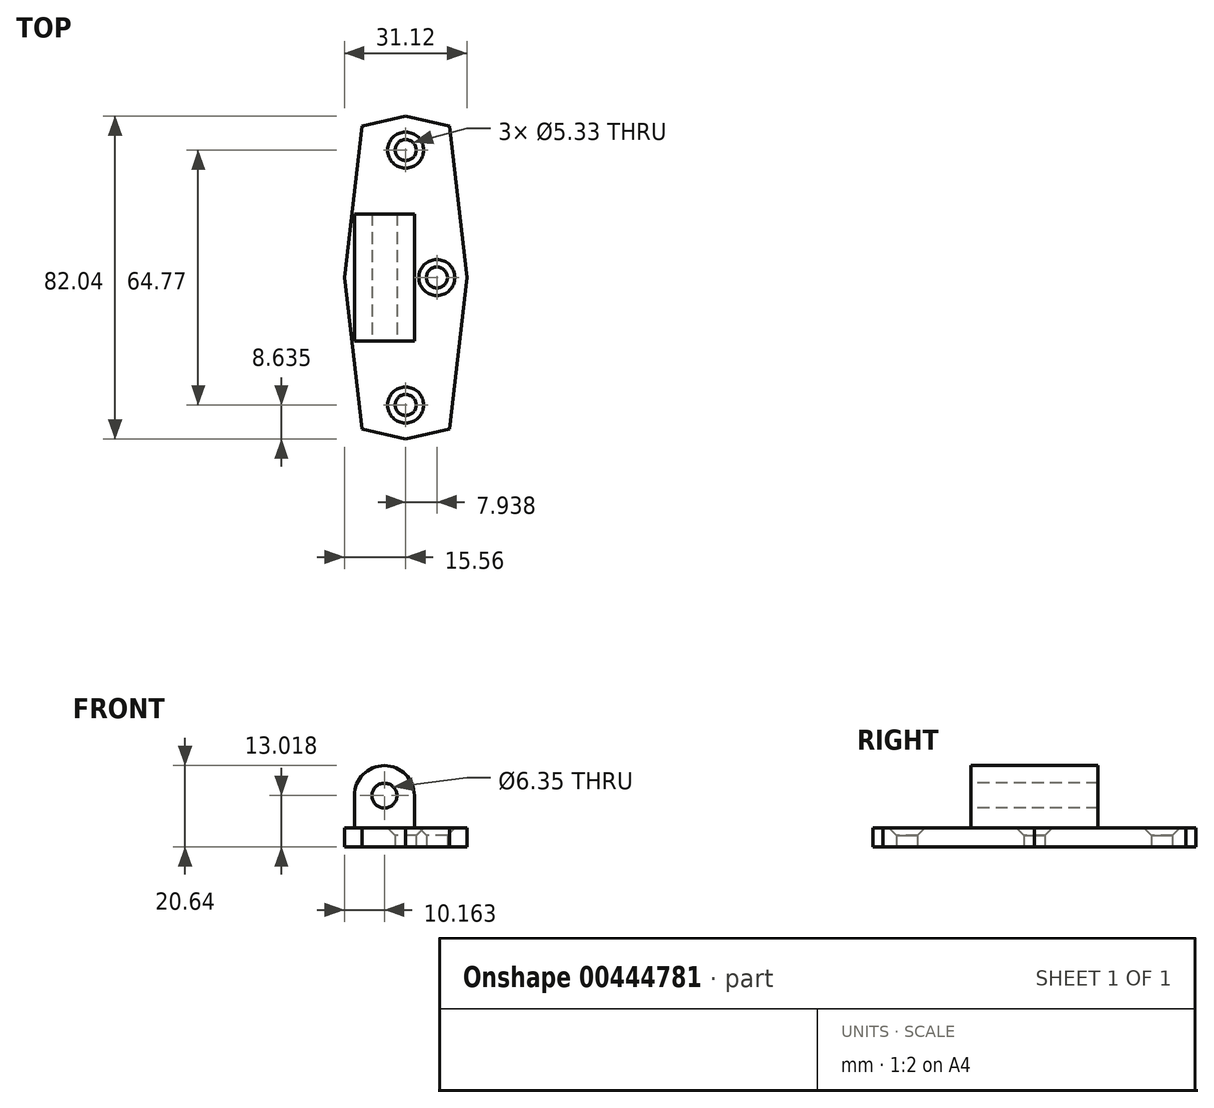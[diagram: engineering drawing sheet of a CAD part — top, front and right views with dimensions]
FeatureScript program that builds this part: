
annotation { "Feature Type Name" : "Feature", "Feature Type Description" : "" }
export const myFeature = defineFeature(function(context is Context, id is Id, definition is map)
    precondition{}
    {
        {
            var Q0;
            Q0=qCreatedBy(makeId("Top.planeOp"),FACE);
            var sketch = newSketch(context, id + "F0", { "sketchPlane" : qUnion([Q0])});
            skLineSegment(sketch, "E0", {"start": v(0, 41.02) * mm, "end": v(0, 41.02) * mm});
            skLineSegment(sketch, "E1", {"start": v(11.11, 41.02) * mm, "end": v(11.11, 41.02) * mm});
            skPoint(sketch, "E2.MirrorCS.end.orphan", {"position": v(0, 0) * mm});
            skPoint(sketch, "E2.MirrorCS.start.orphan", {"position": v(0, 41.02) * mm});
            skPoint(sketch, "E3.MirrorCS.start.orphan", {"position": v(-15.56, 0) * mm});
            skPoint(sketch, "E4", {"position": v(0, 32.39) * mm});
            skPoint(sketch, "E5.MirrorP", {"position": v(0, -32.39) * mm});
            skPoint(sketch, "E6", {"position": v(7.94, 0) * mm});
            skCircle(sketch, "E7", {"center": v(7.94, 0) * mm, "radius": 2.67 * mm});
            skCircle(sketch, "E8", {"center": v(0, 32.39) * mm, "radius": 2.67 * mm});
            skCircle(sketch, "E9", {"center": v(0, -32.39) * mm, "radius": 2.67 * mm});
            skPoint(sketch, "E10", {"position": v(-5.4, 0) * mm});
            skPoint(sketch, "E11", {"position": v(2.22, 0) * mm});
            skPoint(sketch, "E12", {"position": v(-13.02, 0) * mm});
            skPoint(sketch, "E13", {"position": v(2.22, 16.13) * mm});
            skLineSegment(sketch, "E14.bottom", {"start": v(2.22, 16.13) * mm, "end": v(-13.02, 16.13) * mm});
            skLineSegment(sketch, "E14.top", {"start": v(2.22, -16.13) * mm, "end": v(-13.02, -16.13) * mm});
            skLineSegment(sketch, "E14.left", {"start": v(2.22, 16.13) * mm, "end": v(2.22, -16.13) * mm});
            skLineSegment(sketch, "E14.right", {"start": v(-13.02, 16.13) * mm, "end": v(-13.02, -16.13) * mm});
            skPoint(sketch, "E15.end.orphan", {"position": v(-11.11, -38.48) * mm});
            skPoint(sketch, "E16.MirrorCS.end.orphan", {"position": v(11.18, -42.8) * mm});
            skPoint(sketch, "E17.MirrorCS.end.orphan", {"position": v(11.11, -41.02) * mm});
            skPoint(sketch, "E17.MirrorCS.start.orphan", {"position": v(0, -41.02) * mm});
            skLineSegment(sketch, "E18", {"start": v(0, -41.02) * mm, "end": v(11.18, -38.48) * mm});
            skLineSegment(sketch, "E19", {"start": v(0, -41.02) * mm, "end": v(-11.11, -38.48) * mm});
            skPoint(sketch, "E20.MirrorCS.end.orphan", {"position": v(-11.11, -41.02) * mm});
            skLineSegment(sketch, "E21", {"start": v(15.56, 0) * mm, "end": v(11.18, -38.48) * mm});
            skLineSegment(sketch, "E22", {"start": v(-15.56, 0) * mm, "end": v(-11.11, -38.48) * mm});
            skLineSegment(sketch, "E23", {"start": v(-11.11, 41.02) * mm, "end": v(-11.11, 41.02) * mm});
            skLineSegment(sketch, "E24.MirrorCS", {"start": v(15.56, 0) * mm, "end": v(11.18, 38.48) * mm});
            skLineSegment(sketch, "E25.MirrorCS", {"start": v(0, 41.02) * mm, "end": v(11.18, 38.48) * mm});
            skLineSegment(sketch, "E26.MirrorCS", {"start": v(0, 41.02) * mm, "end": v(-11.11, 38.48) * mm});
            skLineSegment(sketch, "E27.MirrorCS", {"start": v(-15.56, 0) * mm, "end": v(-11.11, 38.48) * mm});
            skSolve(sketch);
        }
        {
            var Q0;
            Q0=makeQuery(id+"F0.imprint","IMPRINT",FACE,{"disambiguationData":[TD([[makeQuery(id+"F0.imprint","IMPRINT",EDGE,{"derivedFrom":sQuery(id+"F0.wireOp",EDGE,"E7")}),-1.0]])]});
            extrude(context, id + "F1", {"entities" : qUnion([Q0]), "depth" : 4.76 * mm});
        }
        {
            var Q0;
            Q0=makeQuery(id+"F0.imprint","IMPRINT",FACE,{"disambiguationData":[TD([[makeQuery(id+"F0.imprint","IMPRINT",EDGE,{"derivedFrom":sQuery(id+"F0.wireOp",EDGE,"E14.bottom")}),1.0]])]});
            extrude(context, id + "F2", {"entities" : qUnion([Q0]), "operationType" : NewBodyOperationType.ADD, "depth" : 13.02 * mm});
        }
        {
            var Q0;
            Q0=makeQuery(id+"F2.opExtrude","CAP_FACE",FACE,{"disambiguationData":[OSD([sQuery(id+"F0.wireOp",EDGE,"E14.bottom"),sQuery(id+"F0.wireOp",EDGE,"E14.top"),sQuery(id+"F0.wireOp",EDGE,"E14.left"),sQuery(id+"F0.wireOp",EDGE,"E14.right")])],"isStart":false});
            var sketch = newSketch(context, id + "F3", { "sketchPlane" : qUnion([Q0])});
            skLineSegment(sketch, "E28", {"start": v(2.22, 16.13) * mm, "end": v(-5.4, 16.13) * mm});
            skLineSegment(sketch, "E29", {"start": v(-5.4, 16.13) * mm, "end": v(-5.4, -16.13) * mm});
            skLineSegment(sketch, "E30", {"start": v(-5.4, -16.13) * mm, "end": v(-5.4, -16.13) * mm});
            skLineSegment(sketch, "E31", {"start": v(-5.4, -16.13) * mm, "end": v(2.22, -16.13) * mm});
            skLineSegment(sketch, "E32", {"start": v(2.22, -16.13) * mm, "end": v(2.22, 16.13) * mm});
            skSolve(sketch);
        }
        {
            var Q0;
            {var subQ0=sQuery(id+"F3.wireOp",EDGE,"E29");Q0=makeQuery(id+"F3.imprint","IMPRINT",FACE,{"disambiguationData":[TD([[makeQuery(id+"F3.imprint","IMPRINT",EDGE,{"derivedFrom":subQ0}),-1.0]])]});}
            var Q1;
            Q1=sQuery(id+"F3.wireOp",EDGE,"E29");
            revolve(context, id + "F4", {"operationType" : NewBodyOperationType.ADD, "entities" : qUnion([Q0]), "axis" : qUnion([Q1]), "revolveType" : RevolveType.FULL});
        }
        {
            var Q0;
            {var subQ0=sQuery(id+"F0.wireOp",EDGE,"E14.top");Q0=makeQuery(id+"F4.boolean.opBoolean","MERGE",FACE,{"derivedFrom":[makeQuery(id+"F2.opExtrude","SWEPT_FACE",FACE,{"disambiguationData":[OSD([subQ0])]}),makeQuery(id+"F4.opRevolve","SWEPT_FACE",FACE,{"disambiguationData":[OSD([subQ0])]})]});}
            var sketch = newSketch(context, id + "F5", { "sketchPlane" : qUnion([Q0])});
            skArc(sketch, "E33.0", {"start": v(-8.57, 13.02) * mm, "mid": v(-5.4, 16.2) * mm, "end": v(-2.22, 13.02) * mm});
            skCircle(sketch, "E34", {"center": v(-5.4, 13.02) * mm, "radius": 3.17 * mm});
            skSolve(sketch);
        }
        {
            var Q0;
            {var subQ0=sQuery(id+"F5.wireOp",EDGE,"E34");var subQ1=makeQuery(id+"F5.imprint","IMPRINT",VERTEX,{"disambiguationData":[OD(0.0)],"derivedFrom":subQ0});Q0=makeQuery(id+"F5.imprint","IMPRINT",FACE,{"disambiguationData":[TD([[makeQuery(id+"F5.imprint","IMPRINT",EDGE,{"disambiguationData":[TD([[subQ1,1.0]])],"derivedFrom":subQ0}),1.0]])]});}
            extrude(context, id + "F6", {"entities" : qUnion([Q0]), "operationType" : NewBodyOperationType.REMOVE, "oppositeDirection" : true, "depth" : 32.26 * mm});
        }
        {
            var Q0;
            Q0=makeQuery(id+"F1.opExtrude","CAP_EDGE",EDGE,{"disambiguationData":[OSD([sQuery(id+"F0.wireOp",EDGE,"E9")])],"isStart":false});
            var Q1;
            Q1=makeQuery(id+"F1.opExtrude","CAP_EDGE",EDGE,{"disambiguationData":[OSD([sQuery(id+"F0.wireOp",EDGE,"E7")])],"isStart":false});
            var Q2;
            Q2=makeQuery(id+"F1.opExtrude","CAP_EDGE",EDGE,{"disambiguationData":[OSD([sQuery(id+"F0.wireOp",EDGE,"E8")])],"isStart":false});
            chamfer(context, id + "F7", {"entities" : qUnion([Q0, Q1, Q2]), "width" : 1.9 * mm, "tangentPropagation" : true});
        }
    });
